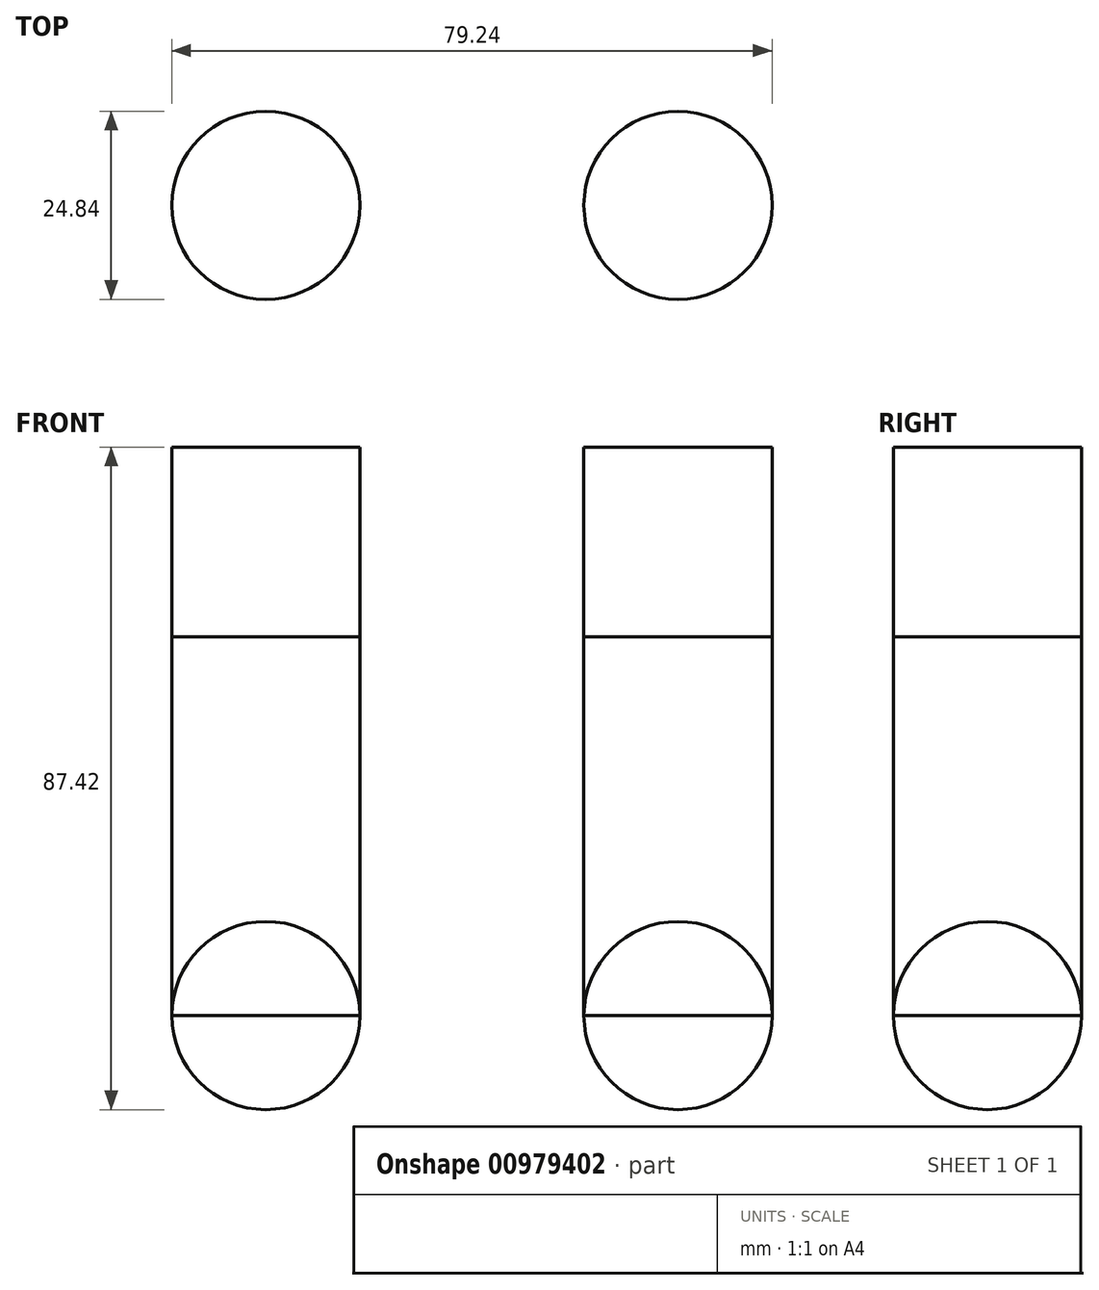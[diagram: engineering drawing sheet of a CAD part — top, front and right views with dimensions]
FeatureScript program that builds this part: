
annotation { "Feature Type Name" : "Feature", "Feature Type Description" : "" }
export const myFeature = defineFeature(function(context is Context, id is Id, definition is map)
    precondition{}
    {
        {
            var Q0;
            Q0=qCreatedBy(makeId("Top.planeOp"),FACE);
            var sketch = newSketch(context, id + "F0", { "sketchPlane" : qUnion([Q0])});
            skLineSegment(sketch, "E0", {"start": v(0, 0) * mm, "end": v(0, 35.7) * mm});
            skLineSegment(sketch, "E1", {"start": v(0, 0) * mm, "end": v(-27.2, 0) * mm});
            skLineSegment(sketch, "E2.MirrorCS", {"start": v(0, 0) * mm, "end": v(27.2, 0) * mm});
            skCircle(sketch, "E3", {"center": v(-27.2, 0) * mm, "radius": 12.42 * mm});
            skCircle(sketch, "E4.MirrorC", {"center": v(27.2, 0) * mm, "radius": 12.42 * mm});
            skLineSegment(sketch, "E5", {"start": v(27.2, 0) * mm, "end": v(39.62, 0) * mm});
            skLineSegment(sketch, "E6", {"start": v(-27.2, 0) * mm, "end": v(-39.62, 0) * mm});
            skSolve(sketch);
        }
        {
            var Q0;
            Q0=qSketchRegion(id+"F0",true);
            extrude(context, id + "F1", {"entities" : qUnion([Q0]), "depth" : 50 * mm, "offsetDistance" : 25.4 * mm});
        }
        {
            var Q0;
            {var subQ0=sQuery(id+"F0.wireOp",EDGE,"E6");Q0=makeQuery(id+"F0.imprint","IMPRINT",FACE,{"disambiguationData":[TD([[makeQuery(id+"F0.imprint","IMPRINT",EDGE,{"derivedFrom":subQ0}),1.0]])]});}
            var Q1;
            {var subQ0=sQuery(id+"F0.wireOp",EDGE,"E5");Q1=makeQuery(id+"F0.imprint","IMPRINT",FACE,{"disambiguationData":[TD([[makeQuery(id+"F0.imprint","IMPRINT",EDGE,{"derivedFrom":subQ0}),-1.0]])]});}
            var Q2;
            Q2=sQuery(id+"F0.wireOp",EDGE,"E1");
            revolve(context, id + "F2", {"surfaceOperationType" : NewSurfaceOperationType.NEW, "entities" : qUnion([Q0, Q1]), "axis" : qUnion([Q2]), "revolveType" : RevolveType.FULL});
        }
        {
            var Q0;
            Q0=makeQuery(id+"F1.opExtrude","CAP_FACE",FACE,{"disambiguationData":[OSD([sQuery(id+"F0.wireOp",EDGE,"E4.MirrorC")])],"isStart":false});
            var Q1;
            Q1=makeQuery(id+"F1.opExtrude","CAP_FACE",FACE,{"disambiguationData":[OSD([sQuery(id+"F0.wireOp",EDGE,"E3")])],"isStart":false});
            extrude(context, id + "F3", {"entities" : qUnion([Q0, Q1]), "depth" : 25 * mm, "offsetDistance" : 25.4 * mm});
        }
    });
